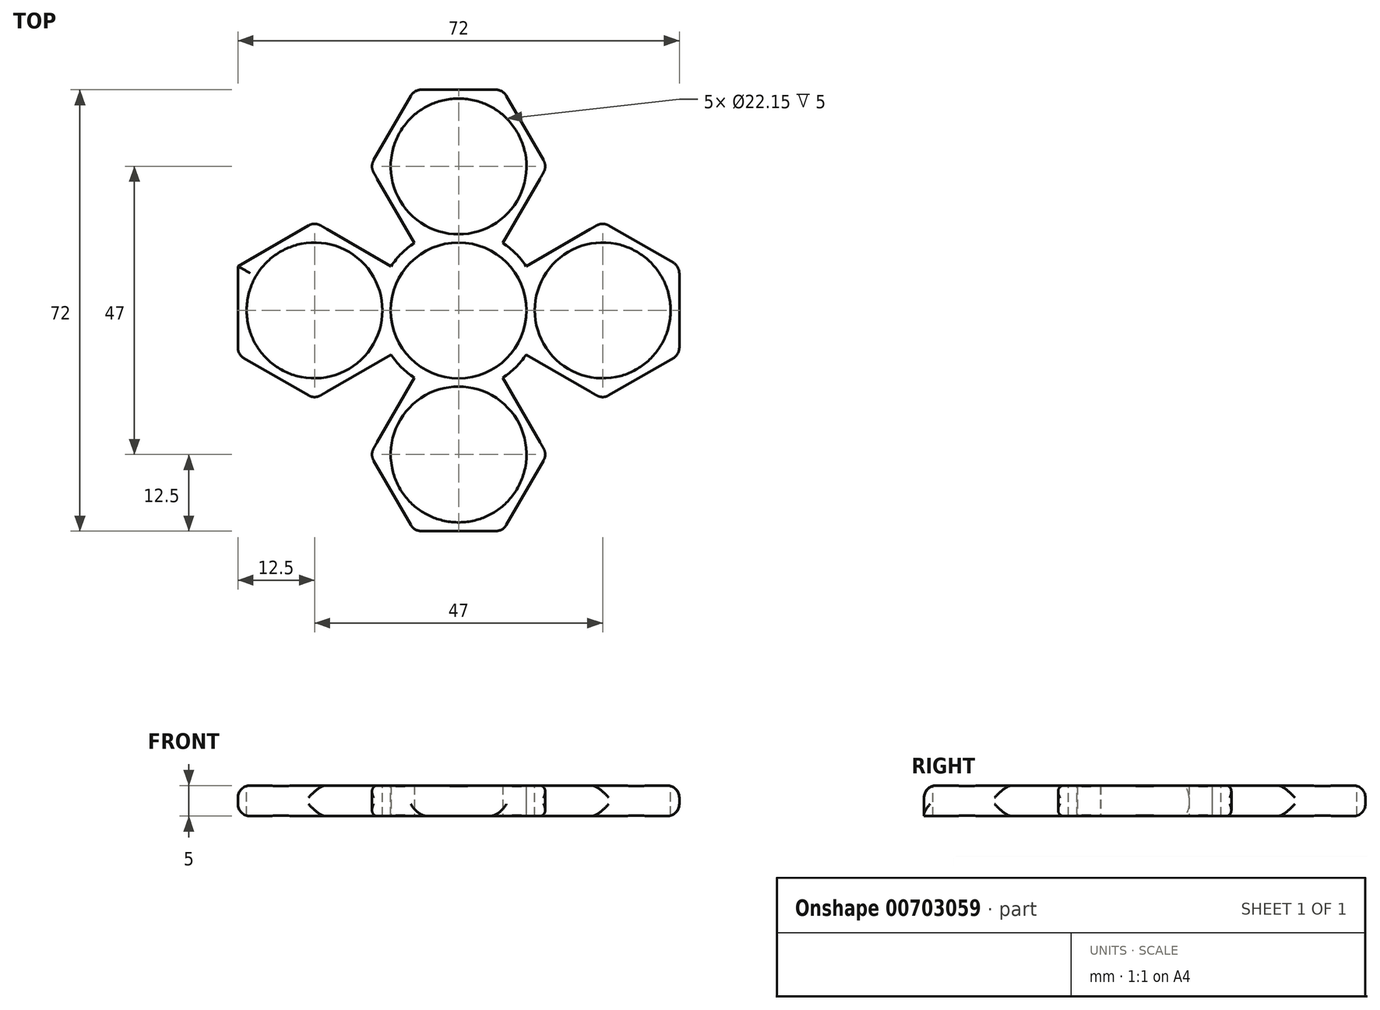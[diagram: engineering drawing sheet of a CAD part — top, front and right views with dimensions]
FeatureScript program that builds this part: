
annotation { "Feature Type Name" : "Feature", "Feature Type Description" : "" }
export const myFeature = defineFeature(function(context is Context, id is Id, definition is map)
    precondition{}
    {
        {
            var Q0;
            Q0=qCreatedBy(makeId("Top.planeOp"),FACE);
            var sketch = newSketch(context, id + "F0", { "sketchPlane" : qUnion([Q0])});
            skCircle(sketch, "E0", {"center": v(0, 0) * mm, "radius": 11 * mm});
            skCircle(sketch, "E1.cCircle", {"center": v(0, 23.5) * mm, "radius": 12.5 * mm, "construction": true});
            skLineSegment(sketch, "E1.0", {"start": v(14.43, 23.5) * mm, "end": v(7.22, 11) * mm});
            skLineSegment(sketch, "E1.1", {"start": v(7.22, 11) * mm, "end": v(-7.22, 11) * mm});
            skLineSegment(sketch, "E1.2", {"start": v(-7.22, 11) * mm, "end": v(-14.43, 23.5) * mm});
            skLineSegment(sketch, "E1.3", {"start": v(-14.43, 23.5) * mm, "end": v(-7.22, 36) * mm});
            skLineSegment(sketch, "E1.4", {"start": v(-7.22, 36) * mm, "end": v(7.22, 36) * mm});
            skLineSegment(sketch, "E1.5", {"start": v(7.22, 36) * mm, "end": v(14.43, 23.5) * mm});
            skPoint(sketch, "E1.0.midPoint", {"position": v(10.83, 17.25) * mm});
            skCircle(sketch, "E2.cCircle", {"center": v(-23.5, 0) * mm, "radius": 12.5 * mm, "construction": true});
            skLineSegment(sketch, "E2.0", {"start": v(-36, -7.22) * mm, "end": v(-36, 7.22) * mm});
            skLineSegment(sketch, "E2.1", {"start": v(-36, 7.22) * mm, "end": v(-23.5, 14.43) * mm});
            skLineSegment(sketch, "E2.2", {"start": v(-23.5, 14.43) * mm, "end": v(-11, 7.22) * mm});
            skLineSegment(sketch, "E2.3", {"start": v(-11, 7.22) * mm, "end": v(-11, -7.22) * mm});
            skLineSegment(sketch, "E2.4", {"start": v(-11, -7.22) * mm, "end": v(-23.5, -14.43) * mm});
            skLineSegment(sketch, "E2.5", {"start": v(-23.5, -14.43) * mm, "end": v(-36, -7.22) * mm});
            skPoint(sketch, "E2.0.midPoint", {"position": v(-36, 0) * mm});
            skCircle(sketch, "E3.cCircle", {"center": v(0, -23.5) * mm, "radius": 12.5 * mm, "construction": true});
            skLineSegment(sketch, "E3.0", {"start": v(-7.22, -11) * mm, "end": v(7.22, -11) * mm});
            skLineSegment(sketch, "E3.1", {"start": v(7.22, -11) * mm, "end": v(14.43, -23.5) * mm});
            skLineSegment(sketch, "E3.2", {"start": v(14.43, -23.5) * mm, "end": v(7.22, -36) * mm});
            skLineSegment(sketch, "E3.3", {"start": v(7.22, -36) * mm, "end": v(-7.22, -36) * mm});
            skLineSegment(sketch, "E3.4", {"start": v(-7.22, -36) * mm, "end": v(-14.43, -23.5) * mm});
            skLineSegment(sketch, "E3.5", {"start": v(-14.43, -23.5) * mm, "end": v(-7.22, -11) * mm});
            skPoint(sketch, "E3.0.midPoint", {"position": v(0, -11) * mm});
            skCircle(sketch, "E4.cCircle", {"center": v(23.5, 0) * mm, "radius": 12.5 * mm, "construction": true});
            skLineSegment(sketch, "E4.0", {"start": v(36, 7.22) * mm, "end": v(36, -7.22) * mm});
            skLineSegment(sketch, "E4.1", {"start": v(36, -7.22) * mm, "end": v(23.5, -14.43) * mm});
            skLineSegment(sketch, "E4.2", {"start": v(23.5, -14.43) * mm, "end": v(11, -7.22) * mm});
            skLineSegment(sketch, "E4.3", {"start": v(11, -7.22) * mm, "end": v(11, 7.22) * mm});
            skLineSegment(sketch, "E4.4", {"start": v(11, 7.22) * mm, "end": v(23.5, 14.43) * mm});
            skLineSegment(sketch, "E4.5", {"start": v(23.5, 14.43) * mm, "end": v(36, 7.22) * mm});
            skPoint(sketch, "E4.0.midPoint", {"position": v(36, 0) * mm});
            skCircle(sketch, "E5", {"center": v(0, 0) * mm, "radius": 13.15 * mm});
            skSolve(sketch);
        }
        {
            var Q0;
            Q0=makeQuery(id+"F0.imprint","IMPRINT",FACE,{"disambiguationData":[TD([[makeQuery(id+"F0.imprint","IMPRINT",EDGE,{"derivedFrom":sQuery(id+"F0.wireOp",EDGE,"E2.0")}),-1.0]])]});
            var Q1;
            {var subQ0=sQuery(id+"F0.wireOp",EDGE,"E0");var subQ1=makeQuery(id+"F0.imprint","INTERSECT",VERTEX,{"derivedFrom":[subQ0,sQuery(id+"F0.wireOp",EDGE,"E1.1")]});Q1=makeQuery(id+"F0.imprint","IMPRINT",FACE,{"disambiguationData":[TD([[makeQuery(id+"F0.imprint","IMPRINT",EDGE,{"disambiguationData":[TD([[subQ1,1.0]])],"derivedFrom":subQ0}),1.0]])]});}
            var Q2;
            {var subQ0=sQuery(id+"F0.wireOp",EDGE,"E5");var subQ1=sQuery(id+"F0.wireOp",EDGE,"E2.3");var subQ2=makeQuery(id+"F0.imprint","INTERSECT",VERTEX,{"disambiguationData":[OD(0.0)],"derivedFrom":[subQ1,subQ0]});Q2=makeQuery(id+"F0.imprint","IMPRINT",FACE,{"disambiguationData":[TD([[makeQuery(id+"F0.imprint","IMPRINT",EDGE,{"disambiguationData":[TD([[subQ2,-1.0]])],"derivedFrom":subQ1}),-1.0]])]});}
            var Q3;
            {var subQ5=sQuery(id+"F0.wireOp",EDGE,"E1.0");Q3=makeQuery(id+"F0.imprint","IMPRINT",FACE,{"disambiguationData":[TD([[makeQuery(id+"F0.imprint","IMPRINT",EDGE,{"derivedFrom":subQ5}),-1.0]])]});}
            var Q4;
            {var subQ0=sQuery(id+"F0.wireOp",EDGE,"E3.1");Q4=makeQuery(id+"F0.imprint","IMPRINT",FACE,{"disambiguationData":[TD([[makeQuery(id+"F0.imprint","IMPRINT",EDGE,{"derivedFrom":subQ0}),-1.0]])]});}
            var Q5;
            {var subQ0=sQuery(id+"F0.wireOp",EDGE,"E1.1");var subQ1=sQuery(id+"F0.wireOp",EDGE,"E0");var subQ2=makeQuery(id+"F0.imprint","INTERSECT",VERTEX,{"derivedFrom":[subQ1,subQ0]});Q5=makeQuery(id+"F0.imprint","IMPRINT",FACE,{"disambiguationData":[TD([[makeQuery(id+"F0.imprint","IMPRINT",EDGE,{"disambiguationData":[TD([[subQ2,1.0]])],"derivedFrom":subQ1}),-1.0]])]});}
            var Q6;
            Q6=makeQuery(id+"F0.imprint","IMPRINT",FACE,{"disambiguationData":[TD([[makeQuery(id+"F0.imprint","IMPRINT",EDGE,{"derivedFrom":sQuery(id+"F0.wireOp",EDGE,"E4.0")}),-1.0]])]});
            var Q7;
            {var subQ0=sQuery(id+"F0.wireOp",EDGE,"E5");var subQ1=sQuery(id+"F0.wireOp",EDGE,"E4.3");var subQ2=makeQuery(id+"F0.imprint","INTERSECT",VERTEX,{"disambiguationData":[OD(0.0)],"derivedFrom":[subQ1,subQ0]});Q7=makeQuery(id+"F0.imprint","IMPRINT",FACE,{"disambiguationData":[TD([[makeQuery(id+"F0.imprint","IMPRINT",EDGE,{"disambiguationData":[TD([[subQ2,-1.0]])],"derivedFrom":subQ1}),-1.0]])]});}
            var Q8;
            {var subQ0=sQuery(id+"F0.wireOp",EDGE,"E5");var subQ1=sQuery(id+"F0.wireOp",EDGE,"E3.0");var subQ2=makeQuery(id+"F0.imprint","INTERSECT",VERTEX,{"disambiguationData":[OD(0.0)],"derivedFrom":[subQ1,subQ0]});Q8=makeQuery(id+"F0.imprint","IMPRINT",FACE,{"disambiguationData":[TD([[makeQuery(id+"F0.imprint","IMPRINT",EDGE,{"disambiguationData":[TD([[subQ2,-1.0]])],"derivedFrom":subQ1}),-1.0]])]});}
            var Q9;
            {var subQ0=sQuery(id+"F0.wireOp",EDGE,"E2.3");var subQ1=sQuery(id+"F0.wireOp",EDGE,"E0");var subQ2=makeQuery(id+"F0.imprint","INTERSECT",VERTEX,{"derivedFrom":[subQ1,subQ0]});Q9=makeQuery(id+"F0.imprint","IMPRINT",FACE,{"disambiguationData":[TD([[makeQuery(id+"F0.imprint","IMPRINT",EDGE,{"disambiguationData":[TD([[subQ2,-1.0]])],"derivedFrom":subQ1}),-1.0]])]});}
            var Q10;
            {var subQ0=sQuery(id+"F0.wireOp",EDGE,"E1.1");var subQ1=sQuery(id+"F0.wireOp",EDGE,"E0");var subQ2=makeQuery(id+"F0.imprint","INTERSECT",VERTEX,{"derivedFrom":[subQ1,subQ0]});Q10=makeQuery(id+"F0.imprint","IMPRINT",FACE,{"disambiguationData":[TD([[makeQuery(id+"F0.imprint","IMPRINT",EDGE,{"disambiguationData":[TD([[subQ2,-1.0]])],"derivedFrom":subQ1}),-1.0]])]});}
            var Q11;
            {var subQ0=sQuery(id+"F0.wireOp",EDGE,"E4.3");var subQ1=sQuery(id+"F0.wireOp",EDGE,"E0");var subQ2=makeQuery(id+"F0.imprint","INTERSECT",VERTEX,{"derivedFrom":[subQ1,subQ0]});Q11=makeQuery(id+"F0.imprint","IMPRINT",FACE,{"disambiguationData":[TD([[makeQuery(id+"F0.imprint","IMPRINT",EDGE,{"disambiguationData":[TD([[subQ2,1.0]])],"derivedFrom":subQ1}),-1.0]])]});}
            var Q12;
            {var subQ0=sQuery(id+"F0.wireOp",EDGE,"E5");var subQ1=sQuery(id+"F0.wireOp",EDGE,"E1.1");var subQ2=makeQuery(id+"F0.imprint","INTERSECT",VERTEX,{"disambiguationData":[OD(0.0)],"derivedFrom":[subQ1,subQ0]});Q12=makeQuery(id+"F0.imprint","IMPRINT",FACE,{"disambiguationData":[TD([[makeQuery(id+"F0.imprint","IMPRINT",EDGE,{"disambiguationData":[TD([[subQ2,-1.0]])],"derivedFrom":subQ1}),-1.0]])]});}
            extrude(context, id + "F1", {"entities" : qUnion([Q0, Q1, Q2, Q3, Q4, Q5, Q6, Q7, Q8, Q9, Q10, Q11, Q12]), "depth" : 5 * mm, "offsetDistance" : 25 * mm});
        }
        {
            var Q0;
            Q0=makeQuery(id+"F1.opExtrude","CAP_FACE",FACE,{"disambiguationData":[OSD([sQuery(id+"F0.wireOp",EDGE,"E1.0"),sQuery(id+"F0.wireOp",EDGE,"E1.1"),sQuery(id+"F0.wireOp",EDGE,"E1.2"),sQuery(id+"F0.wireOp",EDGE,"E1.3"),sQuery(id+"F0.wireOp",EDGE,"E1.4"),sQuery(id+"F0.wireOp",EDGE,"E1.5"),sQuery(id+"F0.wireOp",EDGE,"E2.0"),sQuery(id+"F0.wireOp",EDGE,"E2.1"),sQuery(id+"F0.wireOp",EDGE,"E2.2"),sQuery(id+"F0.wireOp",EDGE,"E2.3"),sQuery(id+"F0.wireOp",EDGE,"E2.4"),sQuery(id+"F0.wireOp",EDGE,"E2.5"),sQuery(id+"F0.wireOp",EDGE,"E3.0"),sQuery(id+"F0.wireOp",EDGE,"E3.1"),sQuery(id+"F0.wireOp",EDGE,"E3.2"),sQuery(id+"F0.wireOp",EDGE,"E3.3"),sQuery(id+"F0.wireOp",EDGE,"E3.4"),sQuery(id+"F0.wireOp",EDGE,"E3.5"),sQuery(id+"F0.wireOp",EDGE,"E4.0"),sQuery(id+"F0.wireOp",EDGE,"E4.1"),sQuery(id+"F0.wireOp",EDGE,"E4.2"),sQuery(id+"F0.wireOp",EDGE,"E4.3"),sQuery(id+"F0.wireOp",EDGE,"E4.4"),sQuery(id+"F0.wireOp",EDGE,"E4.5"),sQuery(id+"F0.wireOp",EDGE,"E5")])],"isStart":false});
            var sketch = newSketch(context, id + "F2", { "sketchPlane" : qUnion([Q0])});
            skCircle(sketch, "E6", {"center": v(0, 0) * mm, "radius": 11.07 * mm});
            skCircle(sketch, "E7", {"center": v(0, 23.5) * mm, "radius": 11.07 * mm});
            skCircle(sketch, "E8", {"center": v(23.5, 0) * mm, "radius": 11.07 * mm});
            skCircle(sketch, "E9", {"center": v(-23.5, 0) * mm, "radius": 11.07 * mm});
            skCircle(sketch, "E10", {"center": v(0, -23.5) * mm, "radius": 11.07 * mm});
            skSolve(sketch);
        }
        {
            var Q0;
            Q0 = qSketchRegion(id + "F2", true);
            extrude(context, id + "F3", {"entities" : qUnion([Q0]), "operationType" : NewBodyOperationType.REMOVE, "oppositeDirection" : true, "depth" : 5 * mm, "offsetDistance" : 25 * mm});
        }
        {
            var Q0;
            Q0=makeQuery(id+"F1.opExtrude","SWEPT_EDGE",EDGE,{"disambiguationData":[OSD([sQuery(id+"F0.wireOp",EDGE,"E3.3"),sQuery(id+"F0.wireOp",EDGE,"E3.4")])]});
            var Q1;
            Q1=makeQuery(id+"F1.opExtrude","SWEPT_EDGE",EDGE,{"disambiguationData":[OSD([sQuery(id+"F0.wireOp",EDGE,"E3.2"),sQuery(id+"F0.wireOp",EDGE,"E3.3")])]});
            var Q2;
            Q2=makeQuery(id+"F1.opExtrude","SWEPT_EDGE",EDGE,{"disambiguationData":[OSD([sQuery(id+"F0.wireOp",EDGE,"E3.1"),sQuery(id+"F0.wireOp",EDGE,"E3.2")])]});
            var Q3;
            Q3=makeQuery(id+"F1.opExtrude","SWEPT_EDGE",EDGE,{"disambiguationData":[OSD([sQuery(id+"F0.wireOp",EDGE,"E3.4"),sQuery(id+"F0.wireOp",EDGE,"E3.5")])]});
            var Q4;
            Q4=makeQuery(id+"F1.opExtrude","SWEPT_EDGE",EDGE,{"disambiguationData":[OSD([sQuery(id+"F0.wireOp",EDGE,"E2.4"),sQuery(id+"F0.wireOp",EDGE,"E2.5")])]});
            var Q5;
            Q5=makeQuery(id+"F1.opExtrude","SWEPT_EDGE",EDGE,{"disambiguationData":[OSD([sQuery(id+"F0.wireOp",EDGE,"E2.0"),sQuery(id+"F0.wireOp",EDGE,"E2.5")])]});
            var Q6;
            Q6=makeQuery(id+"F1.opExtrude","SWEPT_EDGE",EDGE,{"disambiguationData":[OSD([sQuery(id+"F0.wireOp",EDGE,"E4.1"),sQuery(id+"F0.wireOp",EDGE,"E4.2")])]});
            var Q7;
            Q7=makeQuery(id+"F1.opExtrude","SWEPT_EDGE",EDGE,{"disambiguationData":[OSD([sQuery(id+"F0.wireOp",EDGE,"E4.0"),sQuery(id+"F0.wireOp",EDGE,"E4.1")])]});
            var Q8;
            Q8=makeQuery(id+"F1.opExtrude","SWEPT_EDGE",EDGE,{"disambiguationData":[OSD([sQuery(id+"F0.wireOp",EDGE,"E1.2"),sQuery(id+"F0.wireOp",EDGE,"E1.3")])]});
            var Q9;
            Q9=makeQuery(id+"F1.opExtrude","SWEPT_EDGE",EDGE,{"disambiguationData":[OSD([sQuery(id+"F0.wireOp",EDGE,"E1.0"),sQuery(id+"F0.wireOp",EDGE,"E1.5")])]});
            var Q10;
            Q10=makeQuery(id+"F1.opExtrude","SWEPT_EDGE",EDGE,{"disambiguationData":[OSD([sQuery(id+"F0.wireOp",EDGE,"E4.0"),sQuery(id+"F0.wireOp",EDGE,"E4.5")])]});
            var Q11;
            Q11=makeQuery(id+"F1.opExtrude","CAP_EDGE",EDGE,{"disambiguationData":[OSD([sQuery(id+"F0.wireOp",EDGE,"E4.0")])],"isStart":false});
            var Q12;
            Q12=makeQuery(id+"F1.opExtrude","CAP_EDGE",EDGE,{"disambiguationData":[OSD([sQuery(id+"F0.wireOp",EDGE,"E4.0")])],"isStart":true});
            var Q13;
            Q13=makeQuery(id+"F1.opExtrude","CAP_EDGE",EDGE,{"disambiguationData":[OSD([sQuery(id+"F0.wireOp",EDGE,"E4.1")])],"isStart":false});
            var Q14;
            Q14=makeQuery(id+"F1.opExtrude","CAP_EDGE",EDGE,{"disambiguationData":[OSD([sQuery(id+"F0.wireOp",EDGE,"E4.1")])],"isStart":true});
            var Q15;
            Q15=makeQuery(id+"F1.opExtrude","CAP_EDGE",EDGE,{"disambiguationData":[OSD([sQuery(id+"F0.wireOp",EDGE,"E3.2")])],"isStart":false});
            var Q16;
            Q16=makeQuery(id+"F1.opExtrude","CAP_EDGE",EDGE,{"disambiguationData":[OSD([sQuery(id+"F0.wireOp",EDGE,"E3.2")])],"isStart":true});
            var Q17;
            Q17=makeQuery(id+"F1.opExtrude","CAP_EDGE",EDGE,{"disambiguationData":[OSD([sQuery(id+"F0.wireOp",EDGE,"E3.3")])],"isStart":false});
            var Q18;
            Q18=makeQuery(id+"F1.opExtrude","CAP_EDGE",EDGE,{"disambiguationData":[OSD([sQuery(id+"F0.wireOp",EDGE,"E3.4")])],"isStart":true});
            var Q19;
            Q19=makeQuery(id+"F1.opExtrude","CAP_EDGE",EDGE,{"disambiguationData":[OSD([sQuery(id+"F0.wireOp",EDGE,"E3.4")])],"isStart":false});
            var Q20;
            Q20=makeQuery(id+"F1.opExtrude","CAP_EDGE",EDGE,{"disambiguationData":[OSD([sQuery(id+"F0.wireOp",EDGE,"E2.5")])],"isStart":true});
            var Q21;
            Q21=makeQuery(id+"F1.opExtrude","CAP_EDGE",EDGE,{"disambiguationData":[OSD([sQuery(id+"F0.wireOp",EDGE,"E2.5")])],"isStart":false});
            var Q22;
            Q22=makeQuery(id+"F1.opExtrude","CAP_EDGE",EDGE,{"disambiguationData":[OSD([sQuery(id+"F0.wireOp",EDGE,"E2.0")])],"isStart":false});
            var Q23;
            Q23=makeQuery(id+"F1.opExtrude","CAP_EDGE",EDGE,{"disambiguationData":[OSD([sQuery(id+"F0.wireOp",EDGE,"E2.0")])],"isStart":true});
            var Q24;
            Q24=makeQuery(id+"F1.opExtrude","CAP_EDGE",EDGE,{"disambiguationData":[OSD([sQuery(id+"F0.wireOp",EDGE,"E2.1")])],"isStart":true});
            var Q25;
            Q25=makeQuery(id+"F1.opExtrude","CAP_EDGE",EDGE,{"disambiguationData":[OSD([sQuery(id+"F0.wireOp",EDGE,"E2.1")])],"isStart":false});
            var Q26;
            Q26=makeQuery(id+"F1.opExtrude","SWEPT_EDGE",EDGE,{"disambiguationData":[OSD([sQuery(id+"F0.wireOp",EDGE,"E2.1"),sQuery(id+"F0.wireOp",EDGE,"E2.2")])]});
            var Q27;
            Q27=makeQuery(id+"F1.opExtrude","CAP_EDGE",EDGE,{"disambiguationData":[OSD([sQuery(id+"F0.wireOp",EDGE,"E1.3")])],"isStart":true});
            var Q28;
            Q28=makeQuery(id+"F1.opExtrude","CAP_EDGE",EDGE,{"disambiguationData":[OSD([sQuery(id+"F0.wireOp",EDGE,"E1.3")])],"isStart":false});
            var Q29;
            Q29=makeQuery(id+"F1.opExtrude","SWEPT_EDGE",EDGE,{"disambiguationData":[OSD([sQuery(id+"F0.wireOp",EDGE,"E1.3"),sQuery(id+"F0.wireOp",EDGE,"E1.4")])]});
            var Q30;
            Q30=makeQuery(id+"F1.opExtrude","SWEPT_EDGE",EDGE,{"disambiguationData":[OSD([sQuery(id+"F0.wireOp",EDGE,"E1.4"),sQuery(id+"F0.wireOp",EDGE,"E1.5")])]});
            var Q31;
            Q31=makeQuery(id+"F1.opExtrude","CAP_EDGE",EDGE,{"disambiguationData":[OSD([sQuery(id+"F0.wireOp",EDGE,"E1.4")])],"isStart":true});
            var Q32;
            Q32=makeQuery(id+"F1.opExtrude","CAP_EDGE",EDGE,{"disambiguationData":[OSD([sQuery(id+"F0.wireOp",EDGE,"E1.4")])],"isStart":false});
            var Q33;
            Q33=makeQuery(id+"F1.opExtrude","CAP_EDGE",EDGE,{"disambiguationData":[OSD([sQuery(id+"F0.wireOp",EDGE,"E1.5")])],"isStart":false});
            var Q34;
            Q34=makeQuery(id+"F1.opExtrude","CAP_EDGE",EDGE,{"disambiguationData":[OSD([sQuery(id+"F0.wireOp",EDGE,"E1.5")])],"isStart":true});
            var Q35;
            Q35=makeQuery(id+"F1.opExtrude","SWEPT_EDGE",EDGE,{"disambiguationData":[OSD([sQuery(id+"F0.wireOp",EDGE,"E4.4"),sQuery(id+"F0.wireOp",EDGE,"E4.5")])]});
            var Q36;
            Q36=makeQuery(id+"F1.opExtrude","CAP_EDGE",EDGE,{"disambiguationData":[OSD([sQuery(id+"F0.wireOp",EDGE,"E4.5")])],"isStart":true});
            var Q37;
            Q37=makeQuery(id+"F1.opExtrude","CAP_EDGE",EDGE,{"disambiguationData":[OSD([sQuery(id+"F0.wireOp",EDGE,"E4.5")])],"isStart":false});
            fillet(context, id + "F4", {"entities" : qUnion([Q0, Q1, Q2, Q3, Q4, Q5, Q6, Q7, Q8, Q9, Q10, Q11, Q12, Q13, Q14, Q15, Q16, Q17, Q18, Q19, Q20, Q21, Q22, Q23, Q24, Q25, Q26, Q27, Q28, Q29, Q30, Q31, Q32, Q33, Q34, Q35, Q36, Q37]), "radius" : 2 * mm, "tangentPropagation" : true, "allowEdgeOverflow" : false});
        }
    });
